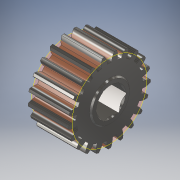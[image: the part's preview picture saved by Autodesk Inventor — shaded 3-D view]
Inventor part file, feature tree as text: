
AUTODESK INVENTOR PART (.ipt)
format: ipt  version: 2018 (Build 220112000, 112)  size: 239,616 bytes
history: native  units: in
note: dims shown in document units (in); Inventor stores cm internally (conversion verified against a paired STEP export)
features: other x3, sketch x1
ambient origin geometry x8: Origin, YZ Plane, XZ Plane, XY Plane, X Axis, Y Axis, Z Axis, Center Point
bodies: Solid1 (feature_tree)
feature tree (4):
  sketch  "Sketch1"  dims[d0=1.05in d1=1.0in d2=0.0in]
  other  "Srf1"
  other  "Cut-Extrude1"
  other  "pitch circle"
